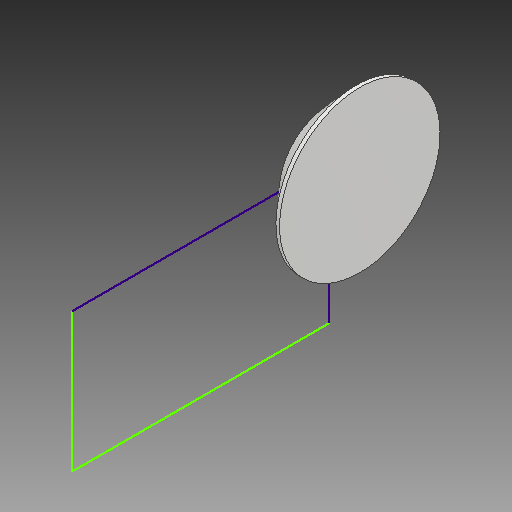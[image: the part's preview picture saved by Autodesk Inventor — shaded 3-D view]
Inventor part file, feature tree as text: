
AUTODESK INVENTOR PART (.ipt)
format: ipt  version: 2018 (Build 220112000, 112)  size: 146,944 bytes
history: native  units: mm
features: sketch x7, extrude x2, revolve x1
ambient origin geometry x8: Origin, YZ Plane, XZ Plane, XY Plane, X Axis, Y Axis, Z Axis, Center Point
bodies: Solid1 (feature_tree)
feature tree (10):
  revolve  "Revolution1"  [1 undecoded]
  extrude  "Extrusion1"  TaperAngle=90.0deg  [1 undecoded]
  sketch  "Sketch4"  dims[d11=24.0mm d12=7.5mm]
  sketch  "Sketch6"  dims[d13=7.4mm]
  sketch  "Sketch7"  dims[d14=10.0mm d15=0.0mm]
  extrude  "Extrusion2"  Depth=7.5mm
  sketch  "Sketch10"  dims[d18=3.0mm d19=0.0mm]
  sketch  "Sketch2"  dims[d4=65.0mm d5=22.0mm]
  sketch  "Sketch3"  dims[d6=40.3mm d7=90.0deg]
  sketch  "Sketch8"  dims[d17=5.0mm]
note: 2 required parameter values undecoded (feature->parameter linkage not recoverable at this tier; creation-order binding heuristic only, values carry confidence <= 0.55)